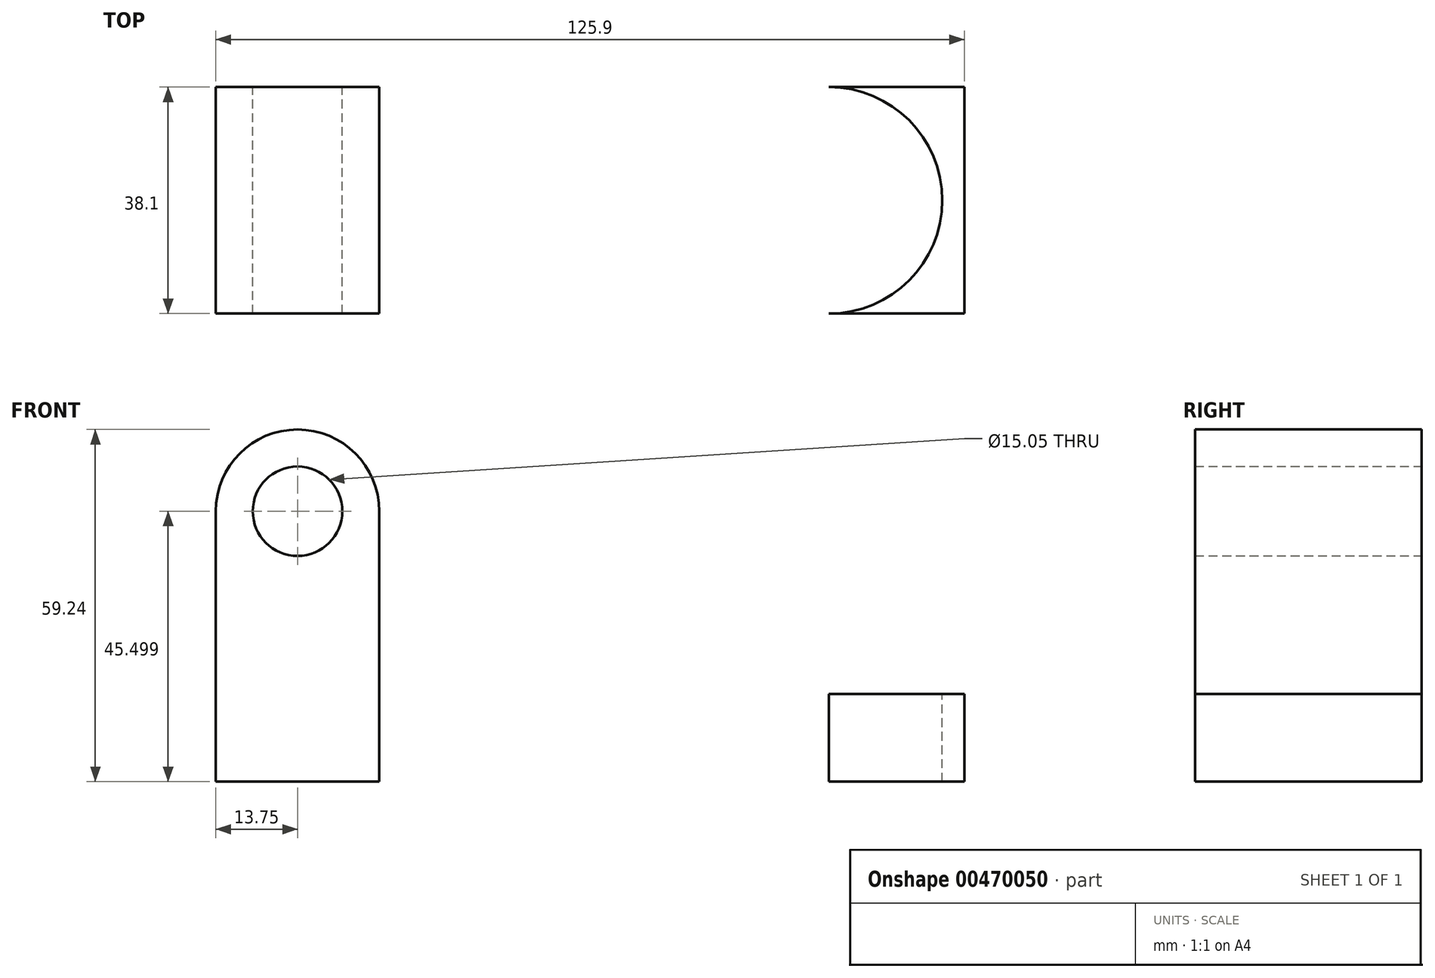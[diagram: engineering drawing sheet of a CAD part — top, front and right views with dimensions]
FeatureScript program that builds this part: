
annotation { "Feature Type Name" : "Feature", "Feature Type Description" : "" }
export const myFeature = defineFeature(function(context is Context, id is Id, definition is map)
    precondition{}
    {
        {
            var Q0;
            Q0=qCreatedBy(makeId("Front.planeOp"),FACE);
            var sketch = newSketch(context, id + "F0", { "sketchPlane" : qUnion([Q0])});
            skLineSegment(sketch, "E0.bottom", {"start": v(62.95, -7.4) * mm, "end": v(-62.95, -7.4) * mm});
            skLineSegment(sketch, "E0.top", {"start": v(62.95, 7.4) * mm, "end": v(-35.45, 7.4) * mm});
            skLineSegment(sketch, "E0.left", {"start": v(62.95, -7.4) * mm, "end": v(62.95, 7.4) * mm});
            skLineSegment(sketch, "E0.right", {"start": v(-62.95, -7.4) * mm, "end": v(-62.95, 7.4) * mm});
            skPoint(sketch, "E0.middle", {"position": v(0, 0) * mm});
            skLineSegment(sketch, "E1", {"start": v(-62.95, 7.4) * mm, "end": v(-62.95, 38.1) * mm});
            skLineSegment(sketch, "E2", {"start": v(-35.45, 38.1) * mm, "end": v(-35.45, 7.4) * mm});
            skArc(sketch, "E3", {"start": v(-35.45, 38.1) * mm, "mid": v(-49.2, 51.85) * mm, "end": v(-62.95, 38.1) * mm});
            skCircle(sketch, "E4", {"center": v(-49.2, 38.1) * mm, "radius": 7.53 * mm});
            skSolve(sketch);
        }
        {
            var Q0;
            Q0 = qSketchRegion(id + "F0", true);
            extrude(context, id + "F1", {"entities" : qUnion([Q0]), "depth" : 38.1 * mm});
        }
        {
            var Q0;
            Q0=makeQuery(id+"F1.opExtrude","SWEPT_FACE",FACE,{"disambiguationData":[OSD([sQuery(id+"F0.wireOp",EDGE,"E0.top")])]});
            var sketch = newSketch(context, id + "F2", { "sketchPlane" : qUnion([Q0])});
            skLineSegment(sketch, "E5", {"start": v(40.2, 0) * mm, "end": v(40.2, -38.1) * mm, "construction": true});
            skArc(sketch, "E6", {"start": v(40.2, 0) * mm, "mid": v(59.24, -19.05) * mm, "end": v(40.2, -38.1) * mm});
            skArc(sketch, "E7", {"start": v(40.2, -27.4) * mm, "mid": v(48.54, -19.05) * mm, "end": v(40.2, -10.7) * mm});
            skLineSegment(sketch, "E8", {"start": v(0, 0) * mm, "end": v(0, -38.1) * mm, "construction": true});
            skArc(sketch, "E9", {"start": v(0, -10.7) * mm, "mid": v(-8.35, -19.05) * mm, "end": v(0, -27.4) * mm});
            skLineSegment(sketch, "E10", {"start": v(0, -10.7) * mm, "end": v(40.2, -10.7) * mm});
            skLineSegment(sketch, "E11", {"start": v(40.2, -27.4) * mm, "end": v(0, -27.4) * mm});
            skSolve(sketch);
        }
        {
            var Q0;
            Q0 = qSketchRegion(id + "F2", true);
            extrude(context, id + "F3", {"entities" : qUnion([Q0]), "operationType" : NewBodyOperationType.REMOVE, "endBound" : BoundingType.THROUGH_ALL, "oppositeDirection" : true, "depth" : 25.4 * mm});
        }
        {
            var Q0;
            {var subQ0=sQuery(id+"F2.wireOp",EDGE,"E6");Q0=makeQuery(id+"F2.imprint","IMPRINT",FACE,{"disambiguationData":[TD([[makeQuery(id+"F2.imprint","IMPRINT",EDGE,{"derivedFrom":subQ0}),1.0]])]});}
            extrude(context, id + "F4", {"entities" : qUnion([Q0]), "operationType" : NewBodyOperationType.REMOVE, "endBound" : BoundingType.THROUGH_ALL, "oppositeDirection" : true, "depth" : 25.4 * mm});
        }
    });
